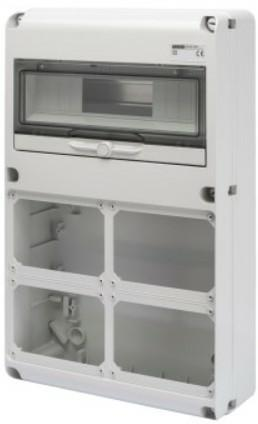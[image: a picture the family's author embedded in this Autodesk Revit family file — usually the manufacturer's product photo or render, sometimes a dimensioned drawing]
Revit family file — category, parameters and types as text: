
# Revit family: Building-QuadriIEC309-GEWISS-68QDIN-QUADRI-PRESE-14MOD_4PRESE_IB_ORIZ
name_source: partatom
category: Apparecchi elettrici
units: mm (PartAtom-declared; Revit-internal decimal feet)

## family parameters
Condiviso = No
Host = Superficie
Mantenere orientamento annotazione = Sì
Punto di calcolo locali = Sì
Quota connettore circolare = Usa diametro
Taglio con vuoti quando caricato = No
Tipo di parte = Normale

## types (1)
- GW68009N - Q-DIN 14M 4FLANGE PR.BL.OR.SBF IP65
    Catalogo = BUILDING
    Catalogo Serie = 68 QDIN
    Classe isolamento = II
    Codice EAN = 8011564744806
    Codice Electrocod = 2242
    Colore = Grigio RAL 7035
    Conformità normativa = EN 60208 - EN 60670-1 - IEC 60670-24
    Descrizione = Q-DIN 14M 4FLANGE PR.BL.OR.SBF IP65
    Glow Wire Test = 650°C
    Grado di protezione = IP65
    IDF = 14bb87c4-b455-42ea-803a-ce3560bfe06d
    IDT = 99915e0d-742e-4288-be31-3e8f2e4a73df
    Immagine tipo = GW68009N.jpg
    L_Moduli = 266 mm  [stored 0.872703 ft]
    Modello = GW68009N
    N. IEC 309/IB alloggiabili = 4 IB Orizz. 16/32 A SBF IP44
    N. coperchi ciechi in dotazione = 2 IB 16/32 A
    N. flange in dotazione = 2 IB 16/32 A
    N. mod. EN 50022 = 14
    N. prese IB alloggiabili: = 4 IB Orizz. 16/32 A SBF IP44
    N. prese alloggiabili = 4 IB Orizz. 16/32 A SBF IP44
    N_Moduli = 14 mm  [stored 0.0459318 ft]
    POMELLO = bianco
    PRESA = rosso
    Potenza dissipabile A (W) = 24
    Potenza dissipabile B (W) = 64
    Produttore = GEWISS S.p.A.
    Prospetto di default = 1219 mm
    Resistenza agli urti = IK08
    SEO = Quadretto
    STRUTTURA = RAL - 7035
    STRUTTURA ALTA = Poche
    Scheda Tecnica = https://www.gewiss.com
    Spostamento_S = 1000 mm  [stored 3.28084 ft]
    Temperatura di funzionamento = -25 ÷ +40 °C
    Temperatura di utilizzo = -25 +40 °C
    Termopressione con biglia = 70 °C
    Tipo versione = Vuoto
    Tipologia di installazione = Da parete
    URL = https://www.gewiss.com
    VETRO = Vetro
    Versione file RFA = 21.5

note: [stored X ft] marks values corroborated as IEEE doubles in the binary element streams (Revit-internal decimal feet)

## geometry (parser evidence)
native form markers: Sweep x4
no freeform markers — native parametric forms only
